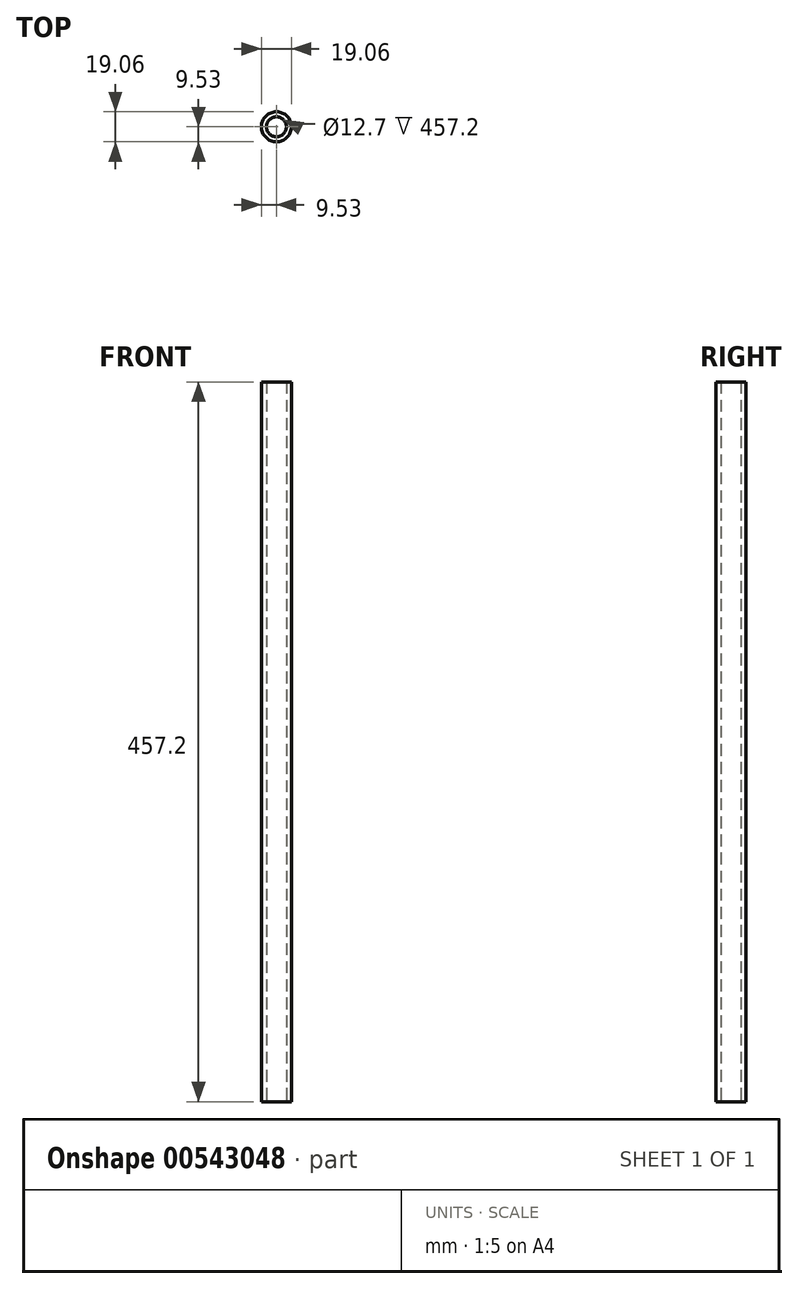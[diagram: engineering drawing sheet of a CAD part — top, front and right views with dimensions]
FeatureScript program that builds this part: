
annotation { "Feature Type Name" : "Feature", "Feature Type Description" : "" }
export const myFeature = defineFeature(function(context is Context, id is Id, definition is map)
    precondition{}
    {
        {
            var Q0;
            Q0=qCreatedBy(makeId("Top.planeOp"),FACE);
            var sketch = newSketch(context, id + "F0", { "sketchPlane" : qUnion([Q0])});
            skCircle(sketch, "E0", {"center": v(0, 0) * mm, "radius": 9.53 * mm});
            skCircle(sketch, "E1", {"center": v(0, 0) * mm, "radius": 6.35 * mm});
            skSolve(sketch);
        }
        {
            var Q0;
            Q0=qSketchRegion(id+"F0",true);
            extrude(context, id + "F1", {"entities" : qUnion([Q0]), "depth" : 457.2 * mm, "offsetDistance" : 25.4 * mm});
        }
    });
